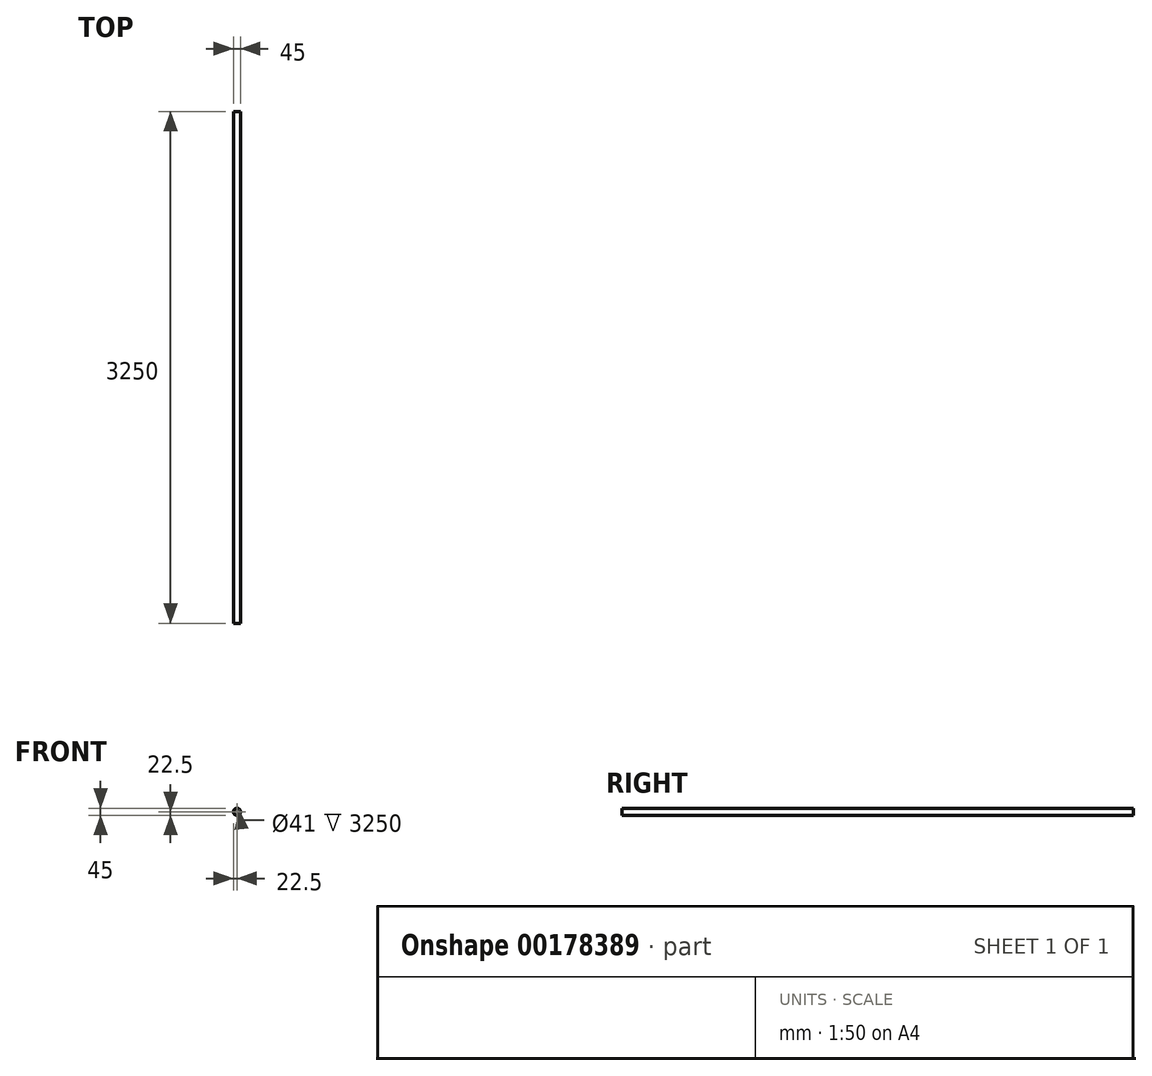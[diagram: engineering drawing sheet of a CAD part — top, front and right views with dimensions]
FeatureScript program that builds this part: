
annotation { "Feature Type Name" : "Feature", "Feature Type Description" : "" }
export const myFeature = defineFeature(function(context is Context, id is Id, definition is map)
    precondition{}
    {
        {
            var Q0;
            Q0=qCreatedBy(makeId("Front.planeOp"),FACE);
            var sketch = newSketch(context, id + "F0", { "sketchPlane" : qUnion([Q0])});
            skCircle(sketch, "E0", {"center": v(0, 0) * mm, "radius": 22.5 * mm});
            skCircle(sketch, "E1.0", {"center": v(0, 0) * mm, "radius": 20.5 * mm});
            skSolve(sketch);
        }
        {
            var Q0;
            Q0=makeQuery(id+"F0.imprint","IMPRINT",FACE,{"disambiguationData":[TD([[makeQuery(id+"F0.imprint","IMPRINT",EDGE,{"derivedFrom":sQuery(id+"F0.wireOp",EDGE,"E0")}),1.0]])]});
            extrude(context, id + "F1", {"entities" : qUnion([Q0]), "depth" : 3250 * mm});
        }
    });
